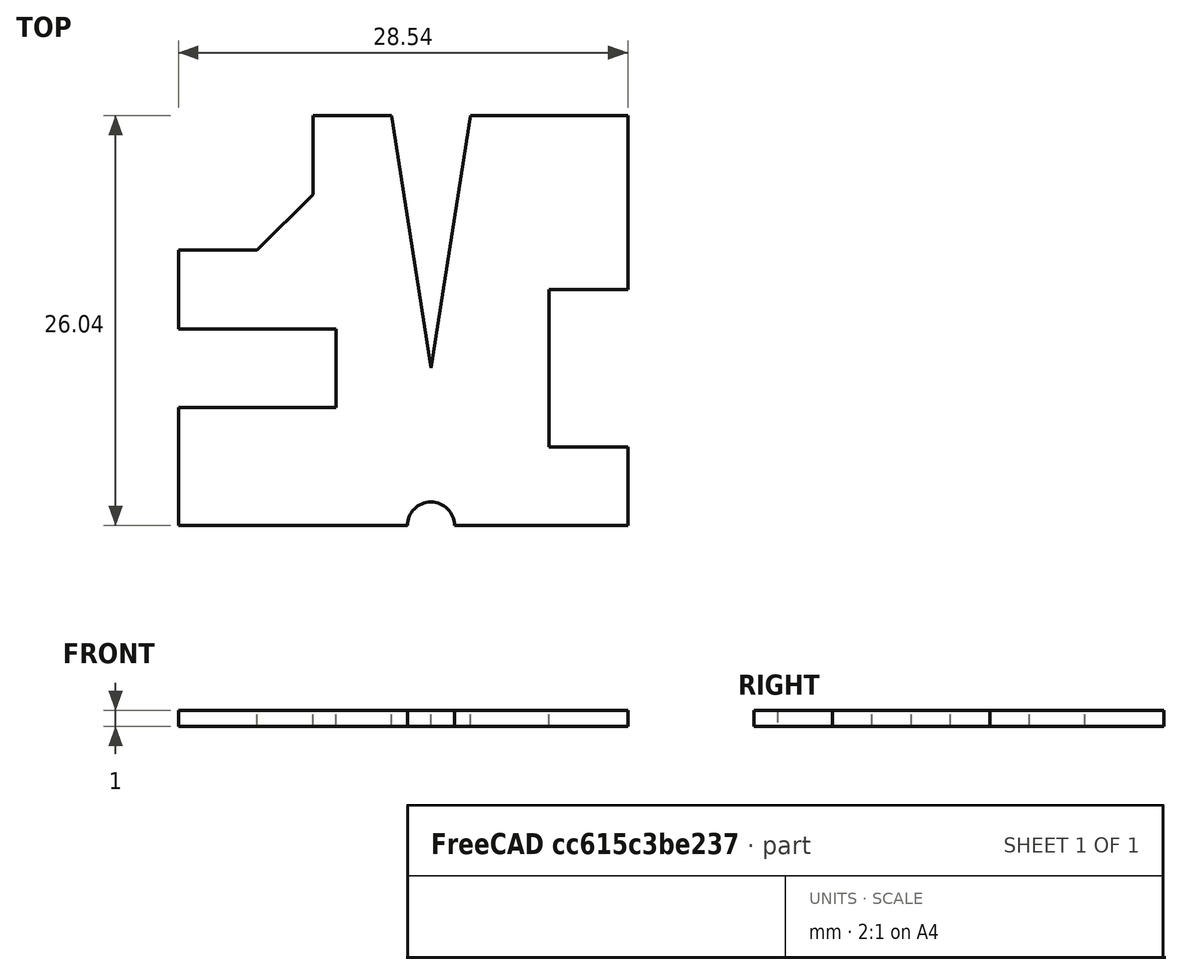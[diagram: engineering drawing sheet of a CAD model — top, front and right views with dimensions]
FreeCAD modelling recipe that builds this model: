
FCSTD DOCUMENT  (FreeCAD 0.17R13327 (Git))
Label: dogbone
License: All rights reserved
LicenseURL: http://en.wikipedia.org/wiki/All_rights_reserved
objects: Sketcher::SketchObject×1, PartDesign::Pad×1, PartDesign::Body×1, App::Part×1
note: 4 computed .brp shape members not serialized (recipe doc carries the construction recipe); baked Part::Feature solids carry a one-line shape summary decoded from their .brp

FEATURE [Sketcher::SketchObject] Sketch
  MapMode = 5
  Support = -> [XY_Plane001]
  sketch-geometry (20):
    g0: LineSegment StartX=-16.0355 StartY=-10 StartZ=0 EndX=-16.0355 EndY=-2.5 EndZ=0
    g1: LineSegment StartX=-16.0355 StartY=-2.5 StartZ=0 EndX=-6.03553 EndY=-2.5 EndZ=0
    g2: LineSegment StartX=-6.03553 StartY=-2.5 StartZ=0 EndX=-6.03553 EndY=2.5 EndZ=0
    g3: LineSegment StartX=-6.03553 StartY=2.5 StartZ=0 EndX=-16.0355 EndY=2.5 EndZ=0
    g4: LineSegment StartX=-16.0355 StartY=2.5 StartZ=0 EndX=-16.0355 EndY=7.5 EndZ=0
    g5: LineSegment StartX=-16.0355 StartY=7.5 StartZ=0 EndX=-11.0355 EndY=7.5 EndZ=0
    g6: LineSegment StartX=-11.0355 StartY=7.5 StartZ=0 EndX=-7.5 EndY=11.0355 EndZ=0
    g7: LineSegment StartX=-7.5 StartY=11.0355 StartZ=0 EndX=-7.5 EndY=16.0355 EndZ=0
    g8: LineSegment StartX=-7.5 StartY=16.0355 StartZ=0 EndX=-2.5 EndY=16.0355 EndZ=0
    g9: LineSegment StartX=-2.5 StartY=16.0355 StartZ=0 EndX=0 EndY=0 EndZ=0
    g10: LineSegment StartX=0 StartY=0 StartZ=0 EndX=2.5 EndY=16.0355 EndZ=0
    g11: LineSegment StartX=2.5 StartY=16.0355 StartZ=0 EndX=12.5 EndY=16.0355 EndZ=0
    g12: LineSegment StartX=12.5 StartY=16.0355 StartZ=0 EndX=12.5 EndY=5 EndZ=0
    g13: LineSegment StartX=12.5 StartY=5 StartZ=0 EndX=7.5 EndY=5 EndZ=0
    g14: LineSegment StartX=7.5 StartY=5 StartZ=0 EndX=7.5 EndY=-5 EndZ=0
    g15: LineSegment StartX=7.5 StartY=-5 StartZ=0 EndX=12.5 EndY=-5 EndZ=0
    g16: LineSegment StartX=12.5 StartY=-5 StartZ=0 EndX=12.5 EndY=-10 EndZ=0
    g17: LineSegment StartX=12.5 StartY=-10 StartZ=0 EndX=1.5 EndY=-10 EndZ=0
    g18: LineSegment StartX=-1.5 StartY=-10 StartZ=0 EndX=-16.0355 EndY=-10 EndZ=0
    g19: ArcOfCircle CenterX=0 CenterY=-10 CenterZ=0 NormalX=0 NormalY=0 NormalZ=1 AngleXU=0 Radius=1.5 StartAngle=0 EndAngle=3.14159
  constraints (60):
    c: Vertical(g0)
    c: Coincident(g0,g1)
    c: Horizontal(g1)
    c: Coincident(g1,g2)
    c: Vertical(g2)
    c: Coincident(g2,g3)
    c: Horizontal(g3)
    c: Coincident(g3,g4)
    c: Vertical(g4)
    c: Coincident(g4,g5)
    c: Horizontal(g5)
    c: Coincident(g5,g6)
    c: Coincident(g6,g7)
    c: Vertical(g7)
    c: Coincident(g7,g8)
    c: Horizontal(g8)
    c: Coincident(g8,g9)
    c: PointOnObject(g9,g-2)
    c: Coincident(g9,g10)
    c: Coincident(g10,g11)
    c: Horizontal(g11)
    c: Coincident(g11,g12)
    c: Vertical(g12)
    c: Coincident(g12,g13)
    c: Coincident(g13,g14)
    c: Vertical(g14)
    c: Coincident(g14,g15)
    c: Horizontal(g15)
    c: Coincident(g15,g16)
    c: Vertical(g16)
    c: Coincident(g18,g0)
    c: Horizontal(g13)
    c: Equal(g13,g15)
    c: Symmetric(g13,g14,g-1)
    c: Symmetric(g8,g10,g-2)
    c: Equal(g3,g1)
    c: Symmetric(g3,g0,g-1)
    c: DistanceX(g15,g15) = 5
    c: Angle(g6) = 0.785398
    c: DistanceY(g14,g14) = 10
    c: DistanceX(g8,g10) = 5
    c: DistanceY(g2,g2) = 5
    c: Distance(g6) = 5
    c: DistanceX(g5,g5) = 5
    c: DistanceY(g7,g7) = 5
    c: DistanceY(g4,g4) = 5
    c: DistanceX(g8,g8) = 5
    c: DistanceX(g3,g3) = 10
    c: DistanceX(g11,g11) = 10
    c: Coincident(g9,g-1)
    c: DistanceY(g16,g16) = 5
    c: PointOnObject(g19,g-2)
    c: PointOnObject(g19,g17)
    c: Coincident(g19,g17)
    c: Coincident(g18,g19)
    c: Symmetric(g17,g18,g19)
    c: Radius(g19) = 1.5
    c: Horizontal(g17)
    c: Horizontal(g18)
    c: Coincident(g17,g16)
FEATURE [PartDesign::Pad] Pad
  Length = 1
  Length2 = 100
  Profile = -> Sketch
  Type = 0
FEATURE [PartDesign::Body] Body
  Origin = -> BodyOrigin
  Tip = -> Pad
FEATURE [App::Part] Part
  Group = -> [Body]
  License = CC BY 3.0
  LicenseURL = http://creativecommons.org/licenses/by/3.0/
  Origin = -> PartOrigin
